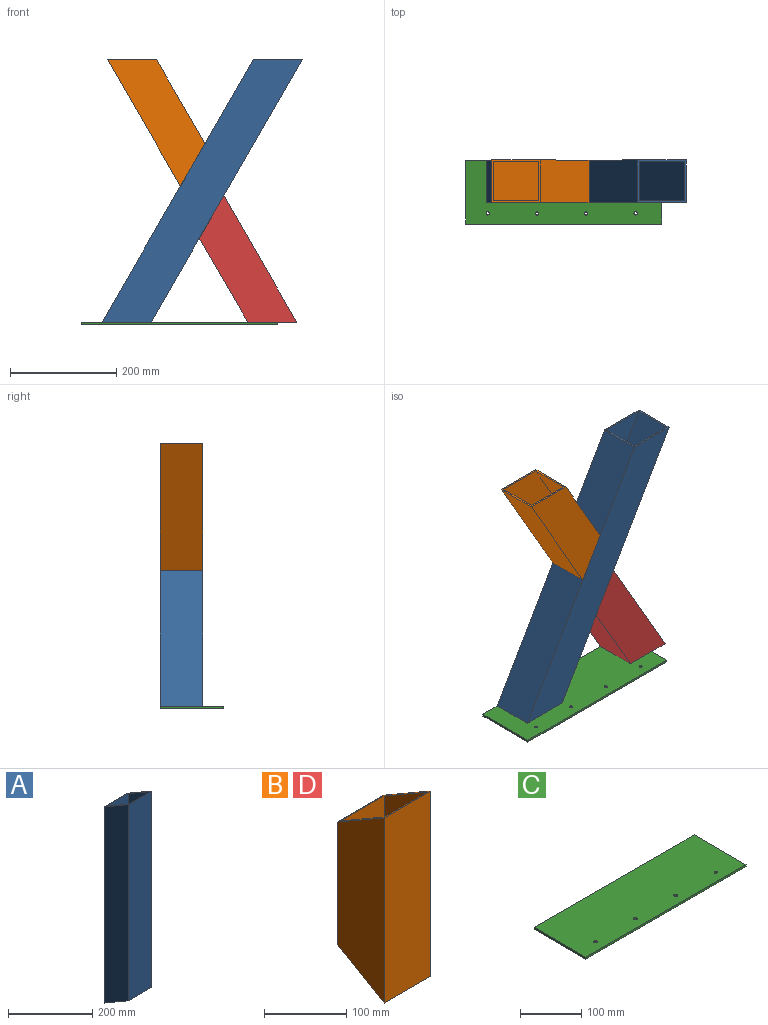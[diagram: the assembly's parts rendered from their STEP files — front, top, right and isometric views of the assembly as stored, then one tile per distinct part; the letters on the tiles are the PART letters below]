
ASSEMBLY  parts=4 mates=8
PART A: 10 faces, bbox 80x80x617.3 mm
  f0: plane 613.86x74mm, normal (-1,0,0), area 42263.8mm2, adj f1,f3,f4,f5
  f1: plane 571.13x74mm, normal (0,-1,0), area 42263.8mm2, adj f0,f2,f4,f5
  f2: plane 613.86x74mm, normal (1,0,0), area 42263.8mm2, adj f1,f3,f4,f5
  f3: plane 571.13x74mm, normal (0,1,0), area 42263.8mm2, adj f0,f2,f4,f5
  f4: plane 80x80mm, normal (0,0.5,0.87), area 1066.9mm2, adj f0,f1,f2,f3,f6,f7,f8,f9
  f5: plane 80x80mm, normal (0,-0.5,-0.87), area 1066.9mm2, adj f0,f1,f2,f3,f6,f7,f8,f9
  f6: plane 617.32x80mm, normal (-1,0,0), area 45690.6mm2, adj f4,f5,f7,f9
  f7: plane 571.13x80mm, normal (0,-1,0), area 45690.6mm2, adj f4,f5,f6,f8
  f8: plane 617.32x80mm, normal (1,0,0), area 45690.6mm2, adj f4,f5,f7,f9
  f9: plane 571.13x80mm, normal (0,1,0), area 45690.6mm2, adj f4,f5,f6,f8
PART B: 10 faces, bbox 80x80x275 mm
  f0: plane 271.54x74mm, normal (-1,0,0), area 16932.1mm2, adj f1,f3,f4,f5
  f1: plane 186.09x74mm, normal (0,-1,0), area 13770.5mm2, adj f0,f2,f4,f5
  f2: plane 271.54x74mm, normal (1,0,0), area 16932.1mm2, adj f1,f3,f4,f5
  f3: plane 271.54x74mm, normal (0,1,0), area 20093.7mm2, adj f0,f2,f4,f5
  f4: plane 80x80mm, normal (0,0.5,0.87), area 1066.9mm2, adj f0,f1,f2,f3,f6,f7,f8,f9
  f5: plane 80x80mm, normal (0,0.5,-0.87), area 1066.9mm2, adj f0,f1,f2,f3,f6,f7,f8,f9
  f6: plane 182.62x80mm, normal (0,1,0), area 14609.9mm2, adj f4,f5,f7,f9
  f7: plane 275x80mm, normal (-1,0,0), area 18305mm2, adj f4,f5,f6,f8
  f8: plane 275x80mm, normal (0,-1,0), area 22000mm2, adj f4,f5,f7,f9
  f9: plane 275x80mm, normal (1,0,0), area 18305mm2, adj f4,f5,f6,f8
PART C: 10 faces, bbox 370x120x4 mm
  f0: plane 120x4mm, normal (-1,0,0), area 480mm2, adj f1,f6,f8,f9
  f1: plane 370x4mm, normal (0,-1,0), area 1480mm2, adj f0,f2,f8,f9
  f2: plane 120x4mm, normal (1,0,0), area 480mm2, adj f1,f6,f8,f9
  f3: cylinder r=3mm len=6mm, axis (0,0,-1), area 75.4mm2, adj f8,f9
  f4: cylinder r=3mm len=6mm, axis (0,0,-1), area 75.4mm2, adj f8,f9
  f5: cylinder r=3mm len=6mm, axis (0,0,-1), area 75.4mm2, adj f8,f9
  f6: plane 370x4mm, normal (0,1,0), area 1480mm2, adj f0,f2,f8,f9
  f7: cylinder r=3mm len=6mm, axis (0,0,-1), area 75.4mm2, adj f8,f9
  f8: plane 370x120mm, normal (0,0,1), area 44286.9mm2, adj f0,f1,f2,f3,f4,f5,f6,f7
  f9: plane 370x120mm, normal (0,0,-1), area 44286.9mm2, adj f0,f1,f2,f3,f4,f5,f6,f7
PART D: same geometry as B
PLACE A rot(axis=(0.25,0.25,0.94),93.8deg) t=(-197.83,251.91,622.74)mm
PLACE B rot(axis=(0.69,0.69,0.19),158.9deg) t=(-256.54,251.91,1157.36)mm
PLACE C t=(-305.59,211.91,658.74)mm fixed
PLACE D rot(axis=(-0.25,-0.25,0.94),93.8deg) t=(100.27,251.91,662.74)mm
MATE planar A.f6 <-> B.f7  axis (0,-1,0) through (-31.95,251.91,910.05)mm
MATE planar A.f9 <-> B.f4  axis (-0.87,0,0.5) through (-124.32,291.91,910.05)mm
MATE planar A.f5 <-> C.f8  axis (0,0,-1) through (-220.92,291.91,662.74)mm
MATE planar B.f5 <-> A.f4  axis (0,0,1) through (-210.35,291.91,1157.36)mm
MATE planar A.f8 <-> C.f6  axis (0,1,0) through (-78.14,331.91,910.05)mm
MATE planar D.f4 <-> A.f7  axis (-0.87,0,0.5) through (-60.33,291.91,860.9)mm
MATE planar D.f5 <-> A.f5  axis (0,0,-1) through (11.36,254.91,662.74)mm
MATE planar D.f7 <-> A.f6  axis (0,-1,0) through (-0.79,251.91,763.17)mm
